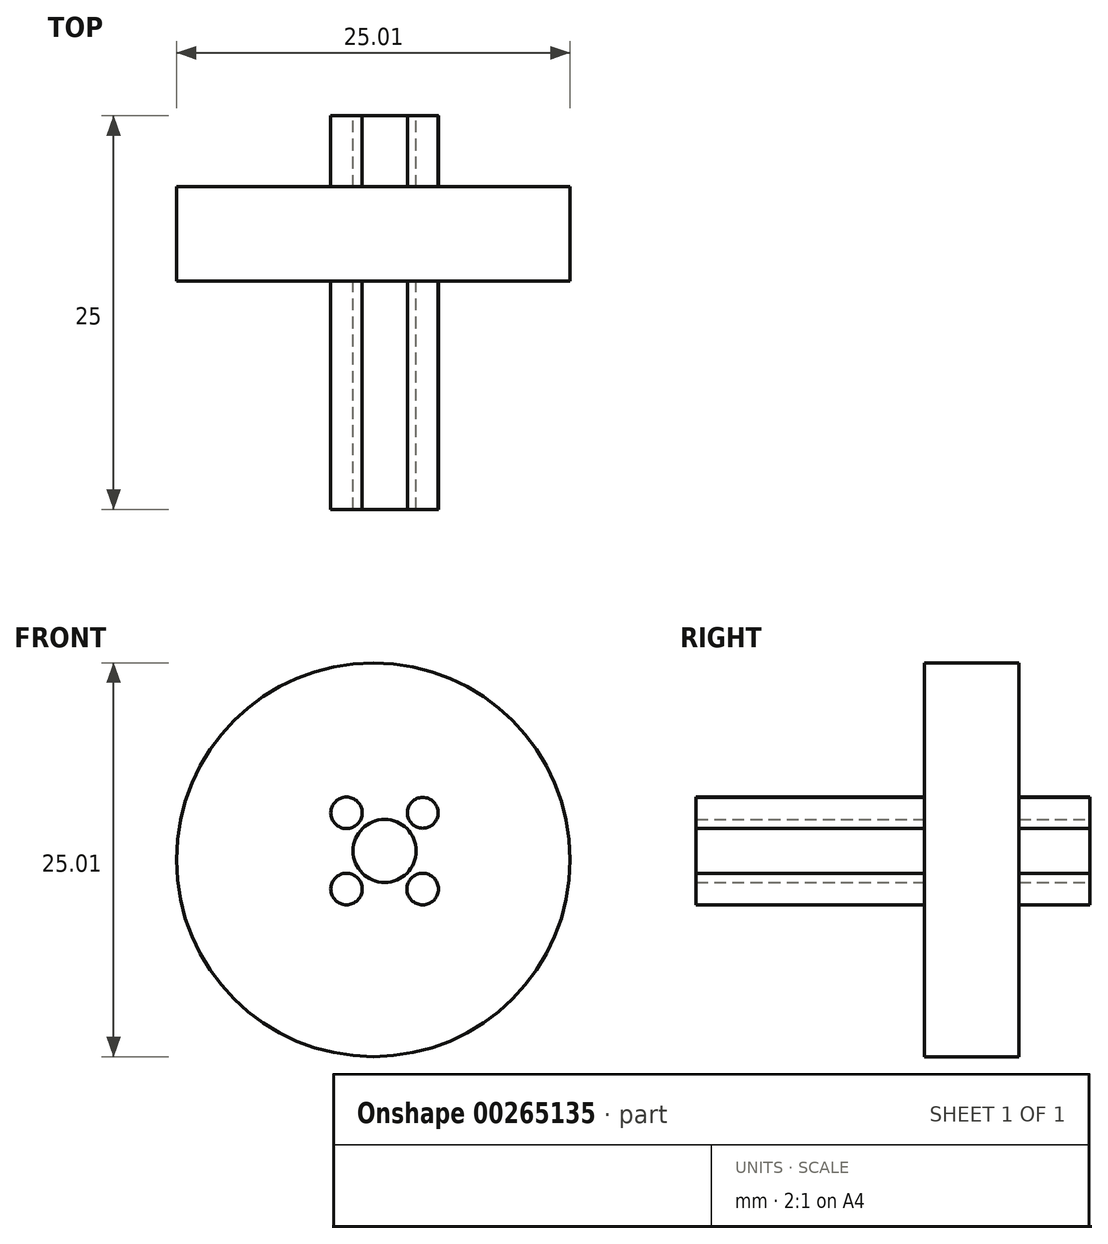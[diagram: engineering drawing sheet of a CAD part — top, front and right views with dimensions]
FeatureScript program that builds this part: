
annotation { "Feature Type Name" : "Feature", "Feature Type Description" : "" }
export const myFeature = defineFeature(function(context is Context, id is Id, definition is map)
    precondition{}
    {
        {
            var Q0;
            Q0=qCreatedBy(makeId("Front.planeOp"),FACE);
            var sketch = newSketch(context, id + "F0", { "sketchPlane" : qUnion([Q0])});
            skCircle(sketch, "E0", {"center": v(-13.58, 22.96) * mm, "radius": 12.5 * mm});
            skPoint(sketch, "E1", {"position": v(-17.1, 34.96) * mm});
            skSolve(sketch);
        }
        {
            var Q0;
            Q0=makeQuery(id+"F0.imprint","IMPRINT",FACE,{"disambiguationData":[TD([[makeQuery(id+"F0.imprint","IMPRINT",EDGE,{"derivedFrom":sQuery(id+"F0.wireOp",EDGE,"E0")}),1.0]])]});
            extrude(context, id + "F1", {"entities" : qUnion([Q0]), "depth" : 6 * mm});
        }
        {
            var Q0;
            Q0=qCreatedBy(makeId("Front.planeOp"),FACE);
            var sketch = newSketch(context, id + "F2", { "sketchPlane" : qUnion([Q0])});
            skCircle(sketch, "E2", {"center": v(-2.49, 2.44) * mm, "radius": 1 * mm});
            skCircle(sketch, "E3", {"center": v(2.35, 2.44) * mm, "radius": 0.98 * mm});
            skCircle(sketch, "E4", {"center": v(-2.49, -2.4) * mm, "radius": 1 * mm});
            skCircle(sketch, "E5", {"center": v(2.35, -2.4) * mm, "radius": 1 * mm});
            skCircle(sketch, "E6", {"center": v(-0.07, 0.02) * mm, "radius": 2 * mm});
            skPoint(sketch, "E7", {"position": v(-2.35, -1.41) * mm});
            skPoint(sketch, "E8", {"position": v(-3.22, 3.12) * mm});
            skPoint(sketch, "E9", {"position": v(1.26, 1.5) * mm});
            skPoint(sketch, "E10", {"position": v(1.8, 1.63) * mm});
            skPoint(sketch, "E11", {"position": v(2.83, -1.52) * mm});
            skSolve(sketch);
        }
        {
            var Q0;
            Q0=makeQuery(id+"F1.opExtrude","SWEPT_BODY",BODY,{"disambiguationData":[OSD([sQuery(id+"F0.wireOp",EDGE,"E0")])]});
            transform(context, id + "F3", {"entities" : qUnion([Q0]), "transformType" : TransformType.TRANSLATION_3D, "dx" : 12.8 * mm, "dy" : -4.5 * mm, "dz" : -23.5 * mm, "makeCopy" : false});
        }
        {
            var Q0;
            Q0 = qSketchRegion(id + "F2", true);
            extrude(context, id + "F4", {"entities" : qUnion([Q0]), "operationType" : NewBodyOperationType.ADD, "depth" : 25 * mm});
        }
    });
